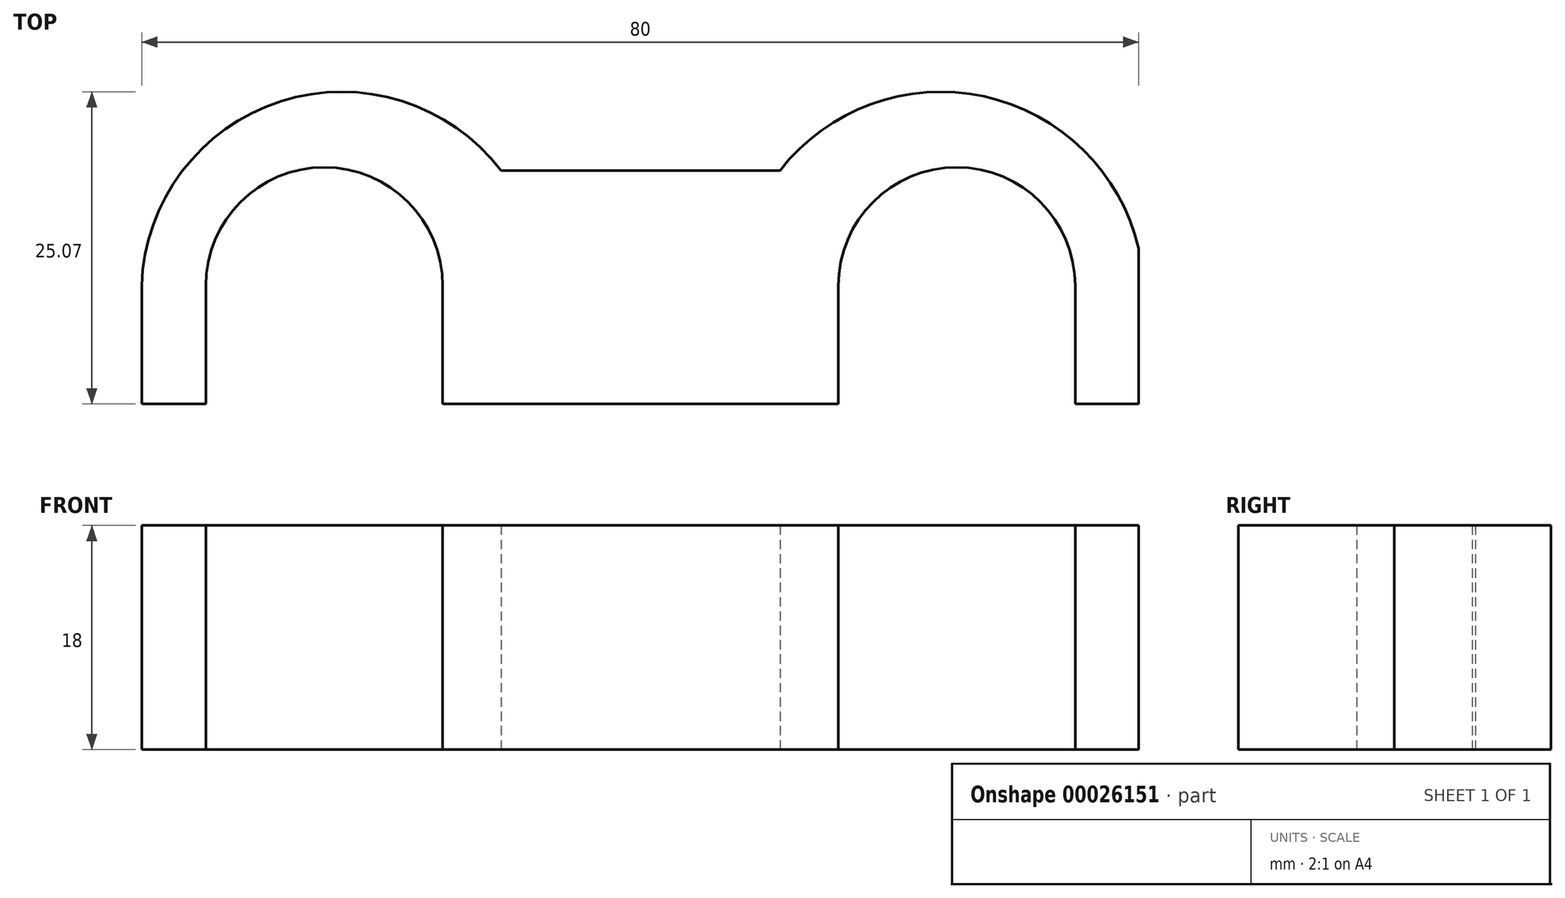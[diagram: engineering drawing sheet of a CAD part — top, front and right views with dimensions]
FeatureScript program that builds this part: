
annotation { "Feature Type Name" : "Feature", "Feature Type Description" : "" }
export const myFeature = defineFeature(function(context is Context, id is Id, definition is map)
    precondition{}
    {
        {
            var Q0;
            Q0=qCreatedBy(makeId("Top.planeOp"),FACE);
            var sketch = newSketch(context, id + "F0", { "sketchPlane" : qUnion([Q0])});
            skLineSegment(sketch, "E0.rect.bottom", {"start": v(40, -12.5) * mm, "end": v(34.9, -12.5) * mm});
            skLineSegment(sketch, "E0.rect.left", {"start": v(40, -12.5) * mm, "end": v(40, 0) * mm});
            skLineSegment(sketch, "E0.rect.right", {"start": v(-40, -12.5) * mm, "end": v(-40, -3) * mm});
            skPoint(sketch, "E0.rect.middle", {"position": v(0, 0) * mm});
            skLineSegment(sketch, "E1", {"start": v(-25.34, -12.5) * mm, "end": v(25.34, -12.5) * mm, "construction": true});
            skPoint(sketch, "E2", {"position": v(0, -12.5) * mm});
            skLineSegment(sketch, "E3", {"start": v(-40, -3) * mm, "end": v(40, -3) * mm, "construction": true});
            skArc(sketch, "E4", {"start": v(-25.35, -12.5) * mm, "mid": v(-25.35, -12.5) * mm, "end": v(-25.34, -12.5) * mm});
            skArc(sketch, "E5", {"start": v(34.9, -3) * mm, "mid": v(25.4, 6.5) * mm, "end": v(15.9, -3) * mm});
            skLineSegment(sketch, "E6", {"start": v(-34.85, -3) * mm, "end": v(-34.85, -12.5) * mm});
            skLineSegment(sketch, "E7", {"start": v(-15.85, -3) * mm, "end": v(-15.85, -12.5) * mm});
            skLineSegment(sketch, "E8", {"start": v(15.9, -3) * mm, "end": v(15.9, -12.5) * mm});
            skLineSegment(sketch, "E9", {"start": v(34.9, -3) * mm, "end": v(34.9, -12.5) * mm});
            skLineSegment(sketch, "E10.trimOffspring", {"start": v(-25.34, -12.5) * mm, "end": v(-25.35, -12.5) * mm});
            skLineSegment(sketch, "E11.trimOffspring", {"start": v(-34.85, -12.5) * mm, "end": v(-40, -12.5) * mm});
            skArc(sketch, "E12.trimOffspring", {"start": v(-15.85, -3) * mm, "mid": v(-25.35, 6.5) * mm, "end": v(-34.85, -3) * mm});
            skLineSegment(sketch, "E13.trimOffspring", {"start": v(25.4, -12.5) * mm, "end": v(25.34, -12.5) * mm});
            skLineSegment(sketch, "E14.trimOffspring", {"start": v(15.9, -12.5) * mm, "end": v(-15.85, -12.5) * mm});
            skArc(sketch, "E15.0", {"start": v(39.9, -3) * mm, "mid": v(25.4, 11.5) * mm, "end": v(10.9, -3) * mm, "construction": true});
            skArc(sketch, "E16.0", {"start": v(-10.85, -3) * mm, "mid": v(-25.35, 11.5) * mm, "end": v(-39.85, -3) * mm, "construction": true});
            skLineSegment(sketch, "E17", {"start": v(-11.17, 6.25) * mm, "end": v(11.21, 6.25) * mm});
            skPoint(sketch, "E18.orphan", {"position": v(-11.17, 0) * mm});
            skPoint(sketch, "E19.orphan", {"position": v(11.21, 0) * mm});
            skArc(sketch, "E20", {"start": v(40, 0) * mm, "mid": v(27.57, 12.2) * mm, "end": v(11.21, 6.25) * mm});
            skPoint(sketch, "E20.second.point", {"position": v(25.6, 12.5) * mm});
            skPoint(sketch, "E20.third.point", {"position": v(40, 0) * mm});
            skArc(sketch, "E21", {"start": v(-11.17, 6.25) * mm, "mid": v(-29.33, 11.63) * mm, "end": v(-40, -4.02) * mm});
            skPoint(sketch, "E21.second.point", {"position": v(-25.35, 12.5) * mm});
            skPoint(sketch, "E22.orphan", {"position": v(-40, 12.5) * mm});
            skPoint(sketch, "E23.end.orphan", {"position": v(-11.17, 12.5) * mm});
            skPoint(sketch, "E24.end.orphan", {"position": v(11.21, 12.5) * mm});
            skPoint(sketch, "E25.orphan", {"position": v(40, 12.5) * mm});
            skSolve(sketch);
        }
        {
            var Q0;
            Q0=makeQuery(id+"F0.imprint","IMPRINT",FACE,{"disambiguationData":[TD([[makeQuery(id+"F0.imprint","IMPRINT",EDGE,{"derivedFrom":sQuery(id+"F0.wireOp",EDGE,"E0.rect.bottom")}),-1.0]])]});
            extrude(context, id + "F1", {"entities" : qUnion([Q0]), "depth" : 18 * mm});
        }
    });
